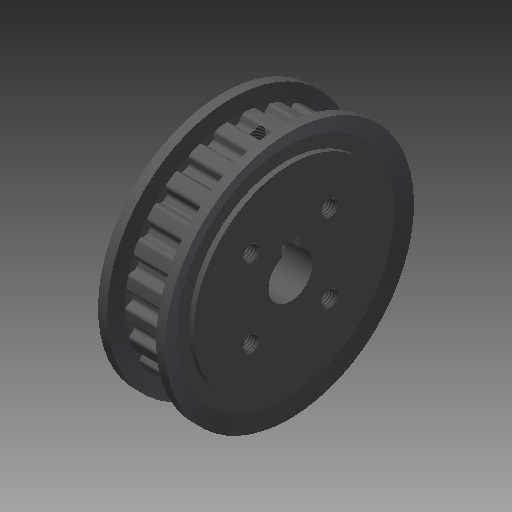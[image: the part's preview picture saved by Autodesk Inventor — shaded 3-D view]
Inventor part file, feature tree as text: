
AUTODESK INVENTOR PART (.ipt)
format: ipt  version: 2017 (Build 210142000, 142)  size: 593,920 bytes
history: native  units: mm
features: other x14, revolve x4, hole x2, extrude x2, thread x2, sketch x2, pattern_linear x1
ambient origin geometry x8: Origin, YZ Plane, XZ Plane, XY Plane, X Axis, Y Axis, Z Axis, Center Point
bodies: Solid1 (feature_tree)
feature tree (27):
  revolve  "Revolution1"  [1 undecoded]
  hole  "Hole1"  [1 undecoded]
  extrude  "Extrusion1"  TaperAngle=360.0deg  [1 undecoded]
  extrude  "Extrusion2"  TaperAngle=360.0deg  [1 undecoded]
  revolve  "Revolution2"  [1 undecoded]
  revolve  "Revolution3"  Angle=360.0deg
  thread  "Thread1"  [1 undecoded]
  revolve  "Revolution4"  [1 undecoded]
  thread  "Thread2"  [1 undecoded]
  hole  "Hole2"  [1 undecoded]
  pattern_linear  "Rectangular Pattern1"  [2 undecoded]
  other  "to_screw1_XY"
  other  "to_screw1_YZ"
  other  "to_screw1_ZX"
  other  "to_screw1_X"
  other  "to_screw1_Y"
  other  "to_screw1_Z"
  other  "to_screw1_Center"
  other  "to_screw2_XY"
  other  "to_screw2_YZ"
  other  "to_screw2_ZX"
  other  "to_screw2_X"
  other  "to_screw2_Y"
  other  "to_screw2_Z"
  other  "to_screw2_Center"
  sketch  "Sketch2"  dims[d0=360.0deg]
  sketch  "Sketch8"  dims[d1=8.0mm d2=6.0mm d3=4.0mm d4=2.0mm d5=90.0deg d6=12.5mm d7=0.0mm d8=7.5mm d9=0.0mm d10=12.5mm d11=0.0mm d12=360.0deg d13=360.0deg d14=14.56mm d15=0.0mm d16=360.0deg d17=15.96mm d18=0.0mm d19=2.459mm d20=6.2705mm d21=3.0mm d22=2.0mm d23=90.0deg d24=8.790148mm d25=120.0deg d26=20.0mm d28=14.142136mm d29=20.0mm d31=14.142136mm d32=0.0mm]
note: 11 required parameter values undecoded (feature->parameter linkage not recoverable at this tier; creation-order binding heuristic only, values carry confidence <= 0.55)